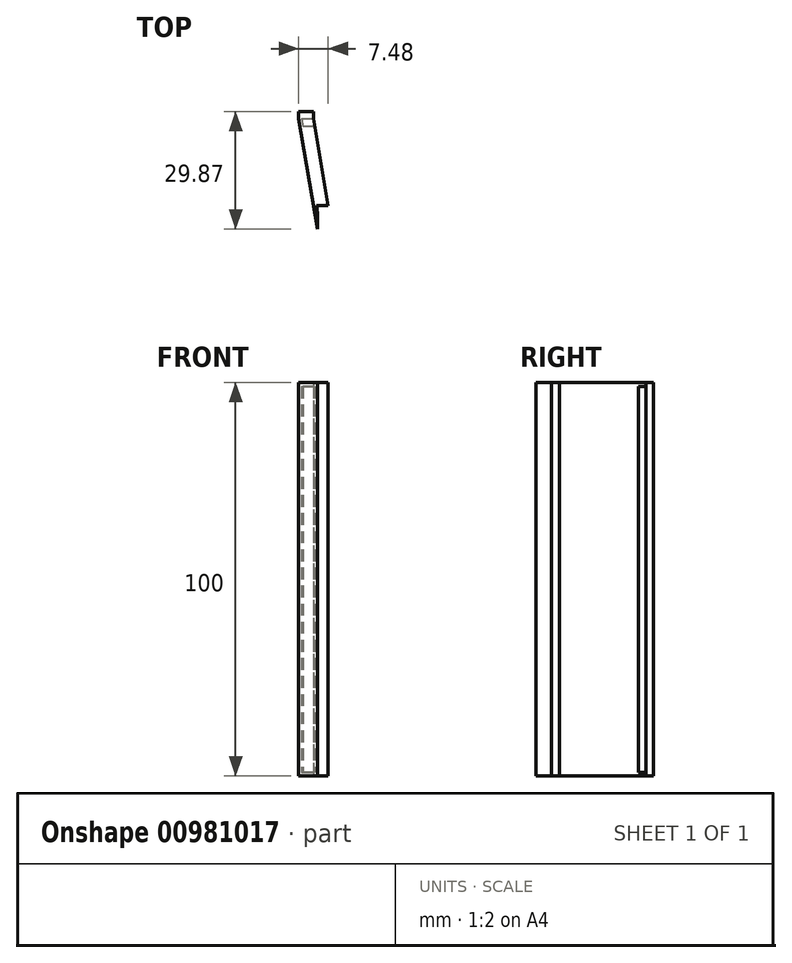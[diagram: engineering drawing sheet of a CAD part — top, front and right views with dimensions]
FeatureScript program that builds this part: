
annotation { "Feature Type Name" : "Feature", "Feature Type Description" : "" }
export const myFeature = defineFeature(function(context is Context, id is Id, definition is map)
    precondition{}
    {
        {
            var Q0;
            Q0=qCreatedBy(makeId("Top.planeOp"),FACE);
            var sketch = newSketch(context, id + "F0", { "sketchPlane" : qUnion([Q0])});
            skLineSegment(sketch, "E0.bottom", {"start": v(-12.5, 2) * mm, "end": v(12.5, 2) * mm});
            skLineSegment(sketch, "E0.top", {"start": v(-12.5, -2) * mm, "end": v(12.5, -2) * mm});
            skLineSegment(sketch, "E0.left", {"start": v(-12.5, 2) * mm, "end": v(-12.5, -2) * mm});
            skLineSegment(sketch, "E0.right", {"start": v(12.5, 2) * mm, "end": v(12.5, -2) * mm});
            skPoint(sketch, "E0.middle", {"position": v(0, 0) * mm});
            skLineSegment(sketch, "E1.left", {"start": v(21.15, 10.87) * mm, "end": v(21.15, 15.48) * mm});
            skLineSegment(sketch, "E2", {"start": v(-5.5, 2) * mm, "end": v(-5.5, -2) * mm});
            skLineSegment(sketch, "E3", {"start": v(-5.5, -2) * mm, "end": v(-3.5, -2) * mm});
            skLineSegment(sketch, "E4", {"start": v(-3.5, -2) * mm, "end": v(-3.5, 2) * mm});
            skLineSegment(sketch, "E5", {"start": v(-3.5, 2) * mm, "end": v(-1.5, 2) * mm});
            skLineSegment(sketch, "E6", {"start": v(-1.5, 2) * mm, "end": v(-1.5, -2) * mm});
            skLineSegment(sketch, "E7", {"start": v(-1.5, -2) * mm, "end": v(0.5, -2) * mm});
            skLineSegment(sketch, "E8", {"start": v(0.5, -2) * mm, "end": v(0.5, 2) * mm});
            skLineSegment(sketch, "E9", {"start": v(0.5, 2) * mm, "end": v(2.5, 2) * mm});
            skLineSegment(sketch, "E10", {"start": v(2.5, 2) * mm, "end": v(2.5, -2) * mm});
            skLineSegment(sketch, "E11", {"start": v(2.5, -2) * mm, "end": v(4.5, -2) * mm});
            skLineSegment(sketch, "E12", {"start": v(4.5, -2) * mm, "end": v(4.5, 2) * mm});
            skLineSegment(sketch, "E13", {"start": v(4.5, 2) * mm, "end": v(6.5, 2) * mm});
            skLineSegment(sketch, "E14", {"start": v(6.5, 2) * mm, "end": v(6.5, -2) * mm});
            skLineSegment(sketch, "E15", {"start": v(0, -2) * mm, "end": v(6.5, -2) * mm});
            skLineSegment(sketch, "E16", {"start": v(0, -2) * mm, "end": v(0, 2) * mm});
            skLineSegment(sketch, "E17", {"start": v(0, 2) * mm, "end": v(8.5, 2) * mm});
            skLineSegment(sketch, "E18", {"start": v(8.5, 2) * mm, "end": v(8.5, -2) * mm});
            skLineSegment(sketch, "E19", {"start": v(8.5, -2) * mm, "end": v(10.5, -2) * mm});
            skLineSegment(sketch, "E20", {"start": v(10.5, -2) * mm, "end": v(10.5, 2) * mm});
            skLineSegment(sketch, "E21", {"start": v(-7.5, 2) * mm, "end": v(-7.5, -2) * mm});
            skLineSegment(sketch, "E22", {"start": v(-7.5, -2) * mm, "end": v(-9.5, -2) * mm});
            skLineSegment(sketch, "E23", {"start": v(-9.5, -2) * mm, "end": v(-9.5, 2) * mm});
            skLineSegment(sketch, "E24", {"start": v(-9.5, 2) * mm, "end": v(-10.4, 2) * mm});
            skLineSegment(sketch, "E25", {"start": v(-12.5, -1.2) * mm, "end": v(12.5, -1.2) * mm});
            skLineSegment(sketch, "E26", {"start": v(-12.5, -2) * mm, "end": v(-17.32, 26) * mm});
            skLineSegment(sketch, "E27", {"start": v(-17.32, 26) * mm, "end": v(-13.63, 26) * mm});
            skLineSegment(sketch, "E28", {"start": v(-13.63, 26) * mm, "end": v(-9.5, 2) * mm});
            skLineSegment(sketch, "E29", {"start": v(-13.29, 24) * mm, "end": v(-16.98, 24) * mm});
            skLineSegment(sketch, "E30", {"start": v(-16.98, 24) * mm, "end": v(-16.63, 22) * mm});
            skLineSegment(sketch, "E31", {"start": v(-16.63, 22) * mm, "end": v(-12.94, 22) * mm});
            skLineSegment(sketch, "E32", {"start": v(-12.94, 22) * mm, "end": v(-12.6, 20) * mm});
            skLineSegment(sketch, "E33", {"start": v(-15.94, 18) * mm, "end": v(-12.25, 18) * mm});
            skLineSegment(sketch, "E34", {"start": v(-12.25, 18) * mm, "end": v(-11.57, 14) * mm});
            skPoint(sketch, "E35.endSnap0", {"position": v(-14.9, 12) * mm});
            skLineSegment(sketch, "E36", {"start": v(-16.29, 20) * mm, "end": v(-12.6, 20) * mm});
            skLineSegment(sketch, "E37", {"start": v(-15.6, 16) * mm, "end": v(-8.68, 16) * mm});
            skLineSegment(sketch, "E38", {"start": v(-15.25, 14) * mm, "end": v(-11.57, 14) * mm});
            skLineSegment(sketch, "E39", {"start": v(-14.9, 12) * mm, "end": v(-11.22, 12) * mm});
            skLineSegment(sketch, "E40", {"start": v(-11.22, 12) * mm, "end": v(-14.9, 12) * mm});
            skLineSegment(sketch, "E41", {"start": v(-14.57, 10) * mm, "end": v(-10.88, 10) * mm});
            skLineSegment(sketch, "E42", {"start": v(-14.22, 8) * mm, "end": v(-10.53, 8) * mm});
            skLineSegment(sketch, "E43", {"start": v(-13.88, 6) * mm, "end": v(-10.19, 6) * mm});
            skLineSegment(sketch, "E44", {"start": v(-13.53, 4) * mm, "end": v(-9.84, 4) * mm});
            skLineSegment(sketch, "E45", {"start": v(-16.63, 26) * mm, "end": v(-12.5, 2) * mm});
            skLineSegment(sketch, "E46", {"start": v(-17.32, 26) * mm, "end": v(-17.32, 27.87) * mm});
            skLineSegment(sketch, "E47", {"start": v(-17.32, 27.87) * mm, "end": v(-13.63, 27.87) * mm});
            skLineSegment(sketch, "E48", {"start": v(-13.63, 27.87) * mm, "end": v(-13.63, 26) * mm});
            skLineSegment(sketch, "E49", {"start": v(12.5, 2) * mm, "end": v(14.56, 2) * mm});
            skLineSegment(sketch, "E50", {"start": v(14.56, 2) * mm, "end": v(12.5, -2) * mm});
            skLineSegment(sketch, "E51", {"start": v(12.5, 0) * mm, "end": v(11.88, -1.2) * mm});
            skLineSegment(sketch, "E52", {"start": v(-9.5, 1.14) * mm, "end": v(-7.5, 1.14) * mm});
            skLineSegment(sketch, "E53", {"start": v(-13.1, 28.79) * mm, "end": v(-8.66, 3) * mm});
            skLineSegment(sketch, "E54", {"start": v(-8.66, 3) * mm, "end": v(16.32, 3) * mm});
            skLineSegment(sketch, "E55", {"start": v(12.5, -3) * mm, "end": v(-13.34, -3) * mm});
            skLineSegment(sketch, "E56", {"start": v(-13.34, -3) * mm, "end": v(-18.81, 28.79) * mm});
            skLineSegment(sketch, "E57", {"start": v(-18.81, 28.79) * mm, "end": v(-13.1, 28.79) * mm});
            skLineSegment(sketch, "E58", {"start": v(16.32, 3) * mm, "end": v(12.5, -3) * mm});
            skSolve(sketch);
        }
        {
            var Q0;
            {var subQ0=sQuery(id+"F0.wireOp",EDGE,"E24");Q0=makeQuery(id+"F0.imprint","IMPRINT",FACE,{"disambiguationData":[TD([[makeQuery(id+"F0.imprint","IMPRINT",EDGE,{"derivedFrom":subQ0}),1.0]])]});}
            var Q1;
            {var subQ0=sQuery(id+"F0.wireOp",EDGE,"E44");var subQ1=sQuery(id+"F0.wireOp",EDGE,"E26");var subQ2=makeQuery(id+"F0.imprint","INTERSECT",VERTEX,{"derivedFrom":[subQ1,subQ0]});Q1=makeQuery(id+"F0.imprint","IMPRINT",FACE,{"disambiguationData":[TD([[makeQuery(id+"F0.imprint","IMPRINT",EDGE,{"disambiguationData":[TD([[subQ2,-1.0]])],"derivedFrom":subQ0}),-1.0]])]});}
            var Q2;
            {var subQ5=sQuery(id+"F0.wireOp",EDGE,"E24");Q2=makeQuery(id+"F0.imprint","IMPRINT",FACE,{"disambiguationData":[TD([[makeQuery(id+"F0.imprint","IMPRINT",EDGE,{"derivedFrom":subQ5}),-1.0]])]});}
            var Q3;
            {var subQ0=sQuery(id+"F0.wireOp",EDGE,"E43");var subQ1=sQuery(id+"F0.wireOp",EDGE,"E26");var subQ2=makeQuery(id+"F0.imprint","INTERSECT",VERTEX,{"derivedFrom":[subQ1,subQ0]});Q3=makeQuery(id+"F0.imprint","IMPRINT",FACE,{"disambiguationData":[TD([[makeQuery(id+"F0.imprint","IMPRINT",EDGE,{"disambiguationData":[TD([[subQ2,1.0]])],"derivedFrom":subQ1}),-1.0]])]});}
            var Q4;
            {var subQ0=sQuery(id+"F0.wireOp",EDGE,"E42");var subQ1=sQuery(id+"F0.wireOp",EDGE,"E28");var subQ2=makeQuery(id+"F0.imprint","INTERSECT",VERTEX,{"derivedFrom":[subQ1,subQ0]});Q4=makeQuery(id+"F0.imprint","IMPRINT",FACE,{"disambiguationData":[TD([[makeQuery(id+"F0.imprint","IMPRINT",EDGE,{"disambiguationData":[TD([[subQ2,-1.0]])],"derivedFrom":subQ1}),-1.0]])]});}
            var Q5;
            {var subQ0=sQuery(id+"F0.wireOp",EDGE,"E42");var subQ1=sQuery(id+"F0.wireOp",EDGE,"E26");var subQ2=makeQuery(id+"F0.imprint","INTERSECT",VERTEX,{"derivedFrom":[subQ1,subQ0]});Q5=makeQuery(id+"F0.imprint","IMPRINT",FACE,{"disambiguationData":[TD([[makeQuery(id+"F0.imprint","IMPRINT",EDGE,{"disambiguationData":[TD([[subQ2,1.0]])],"derivedFrom":subQ1}),-1.0]])]});}
            var Q6;
            {var subQ0=sQuery(id+"F0.wireOp",EDGE,"E41");var subQ1=sQuery(id+"F0.wireOp",EDGE,"E26");var subQ2=makeQuery(id+"F0.imprint","INTERSECT",VERTEX,{"derivedFrom":[subQ1,subQ0]});Q6=makeQuery(id+"F0.imprint","IMPRINT",FACE,{"disambiguationData":[TD([[makeQuery(id+"F0.imprint","IMPRINT",EDGE,{"disambiguationData":[TD([[subQ2,1.0]])],"derivedFrom":subQ1}),-1.0]])]});}
            var Q7;
            {var subQ0=sQuery(id+"F0.wireOp",EDGE,"E40");var subQ1=sQuery(id+"F0.wireOp",EDGE,"E28");var subQ2=makeQuery(id+"F0.imprint","INTERSECT",VERTEX,{"derivedFrom":[subQ1,subQ0]});Q7=makeQuery(id+"F0.imprint","IMPRINT",FACE,{"disambiguationData":[TD([[makeQuery(id+"F0.imprint","IMPRINT",EDGE,{"disambiguationData":[TD([[subQ2,-1.0]])],"derivedFrom":subQ1}),-1.0]])]});}
            var Q8;
            {var subQ1=sQuery(id+"F0.wireOp",EDGE,"E34");var subQ3=sQuery(id+"F0.wireOp",EDGE,"E37");var subQ4=makeQuery(id+"F0.imprint","INTERSECT",VERTEX,{"derivedFrom":[subQ1,subQ3]});Q8=makeQuery(id+"F0.imprint","IMPRINT",FACE,{"disambiguationData":[TD([[makeQuery(id+"F0.imprint","IMPRINT",EDGE,{"disambiguationData":[TD([[subQ4,1.0]])],"derivedFrom":subQ3}),-1.0]])]});}
            var Q9;
            {var subQ3=sQuery(id+"F0.wireOp",EDGE,"E33");var subQ5=sQuery(id+"F0.wireOp",EDGE,"E45");var subQ6=makeQuery(id+"F0.imprint","INTERSECT",VERTEX,{"derivedFrom":[subQ3,subQ5]});Q9=makeQuery(id+"F0.imprint","IMPRINT",FACE,{"disambiguationData":[TD([[makeQuery(id+"F0.imprint","IMPRINT",EDGE,{"disambiguationData":[TD([[subQ6,1.0]])],"derivedFrom":subQ5}),1.0]])]});}
            var Q10;
            {var subQ0=sQuery(id+"F0.wireOp",EDGE,"E40");var subQ1=sQuery(id+"F0.wireOp",EDGE,"E26");var subQ2=makeQuery(id+"F0.imprint","INTERSECT",VERTEX,{"derivedFrom":[subQ1,subQ0]});Q10=makeQuery(id+"F0.imprint","IMPRINT",FACE,{"disambiguationData":[TD([[makeQuery(id+"F0.imprint","IMPRINT",EDGE,{"disambiguationData":[TD([[subQ2,1.0]])],"derivedFrom":subQ1}),-1.0]])]});}
            var Q11;
            {var subQ0=sQuery(id+"F0.wireOp",EDGE,"E38");var subQ1=sQuery(id+"F0.wireOp",EDGE,"E26");var subQ2=makeQuery(id+"F0.imprint","INTERSECT",VERTEX,{"derivedFrom":[subQ1,subQ0]});Q11=makeQuery(id+"F0.imprint","IMPRINT",FACE,{"disambiguationData":[TD([[makeQuery(id+"F0.imprint","IMPRINT",EDGE,{"disambiguationData":[TD([[subQ2,1.0]])],"derivedFrom":subQ1}),-1.0]])]});}
            var Q12;
            {var subQ0=sQuery(id+"F0.wireOp",EDGE,"E37");var subQ1=sQuery(id+"F0.wireOp",EDGE,"E26");var subQ2=makeQuery(id+"F0.imprint","INTERSECT",VERTEX,{"derivedFrom":[subQ1,subQ0]});Q12=makeQuery(id+"F0.imprint","IMPRINT",FACE,{"disambiguationData":[TD([[makeQuery(id+"F0.imprint","IMPRINT",EDGE,{"disambiguationData":[TD([[subQ2,1.0]])],"derivedFrom":subQ1}),-1.0]])]});}
            var Q13;
            {var subQ0=sQuery(id+"F0.wireOp",EDGE,"E33");var subQ1=sQuery(id+"F0.wireOp",EDGE,"E26");var subQ2=makeQuery(id+"F0.imprint","INTERSECT",VERTEX,{"derivedFrom":[subQ1,subQ0]});Q13=makeQuery(id+"F0.imprint","IMPRINT",FACE,{"disambiguationData":[TD([[makeQuery(id+"F0.imprint","IMPRINT",EDGE,{"disambiguationData":[TD([[subQ2,1.0]])],"derivedFrom":subQ1}),-1.0]])]});}
            var Q14;
            {var subQ0=sQuery(id+"F0.wireOp",EDGE,"E33");var subQ1=sQuery(id+"F0.wireOp",EDGE,"E26");var subQ2=makeQuery(id+"F0.imprint","INTERSECT",VERTEX,{"derivedFrom":[subQ1,subQ0]});Q14=makeQuery(id+"F0.imprint","IMPRINT",FACE,{"disambiguationData":[TD([[makeQuery(id+"F0.imprint","IMPRINT",EDGE,{"disambiguationData":[TD([[subQ2,-1.0]])],"derivedFrom":subQ1}),-1.0]])]});}
            var Q15;
            {var subQ1=sQuery(id+"F0.wireOp",EDGE,"E26");var subQ3=sQuery(id+"F0.wireOp",EDGE,"E36");var subQ4=makeQuery(id+"F0.imprint","INTERSECT",VERTEX,{"derivedFrom":[subQ1,subQ3]});Q15=makeQuery(id+"F0.imprint","IMPRINT",FACE,{"disambiguationData":[TD([[makeQuery(id+"F0.imprint","IMPRINT",EDGE,{"disambiguationData":[TD([[subQ4,-1.0]])],"derivedFrom":subQ3}),1.0]])]});}
            var Q16;
            {var subQ0=sQuery(id+"F0.wireOp",EDGE,"E30");Q16=makeQuery(id+"F0.imprint","IMPRINT",FACE,{"disambiguationData":[TD([[makeQuery(id+"F0.imprint","IMPRINT",EDGE,{"derivedFrom":subQ0}),1.0]])]});}
            var Q17;
            {var subQ0=sQuery(id+"F0.wireOp",EDGE,"E27");var subQ5=sQuery(id+"F0.wireOp",EDGE,"E45");var subQ6=makeQuery(id+"F0.imprint","INTERSECT",VERTEX,{"derivedFrom":[subQ0,subQ5]});Q17=makeQuery(id+"F0.imprint","IMPRINT",FACE,{"disambiguationData":[TD([[makeQuery(id+"F0.imprint","IMPRINT",EDGE,{"disambiguationData":[TD([[subQ6,-1.0]])],"derivedFrom":subQ5}),-1.0]])]});}
            var Q18;
            {var subQ0=sQuery(id+"F0.wireOp",EDGE,"E46");Q18=makeQuery(id+"F0.imprint","IMPRINT",FACE,{"disambiguationData":[TD([[makeQuery(id+"F0.imprint","IMPRINT",EDGE,{"derivedFrom":subQ0}),-1.0]])]});}
            var Q19;
            {var subQ0=sQuery(id+"F0.wireOp",EDGE,"E29");var subQ1=sQuery(id+"F0.wireOp",EDGE,"E28");var subQ2=makeQuery(id+"F0.imprint","INTERSECT",VERTEX,{"derivedFrom":[subQ1,subQ0]});Q19=makeQuery(id+"F0.imprint","IMPRINT",FACE,{"disambiguationData":[TD([[makeQuery(id+"F0.imprint","IMPRINT",EDGE,{"disambiguationData":[TD([[subQ2,-1.0]])],"derivedFrom":subQ0}),1.0]])]});}
            extrude(context, id + "F1", {"entities" : qUnion([Q0, Q1, Q2, Q3, Q4, Q5, Q6, Q7, Q8, Q9, Q10, Q11, Q12, Q13, Q14, Q15, Q16, Q17, Q18, Q19]), "depth" : 100 * mm, "offsetDistance" : 25 * mm});
        }
        {
            var Q0;
            {var subQ0=sQuery(id+"F0.wireOp",EDGE,"E33");var subQ1=sQuery(id+"F0.wireOp",EDGE,"E26");var subQ2=makeQuery(id+"F0.imprint","INTERSECT",VERTEX,{"derivedFrom":[subQ1,subQ0]});Q0=makeQuery(id+"F0.imprint","IMPRINT",FACE,{"disambiguationData":[TD([[makeQuery(id+"F0.imprint","IMPRINT",EDGE,{"disambiguationData":[TD([[subQ2,1.0]])],"derivedFrom":subQ1}),-1.0]])]});}
            var Q1;
            {var subQ0=sQuery(id+"F0.wireOp",EDGE,"E34");var subQ5=sQuery(id+"F0.wireOp",EDGE,"E37");var subQ6=makeQuery(id+"F0.imprint","INTERSECT",VERTEX,{"derivedFrom":[subQ0,subQ5]});Q1=makeQuery(id+"F0.imprint","IMPRINT",FACE,{"disambiguationData":[TD([[makeQuery(id+"F0.imprint","IMPRINT",EDGE,{"disambiguationData":[TD([[subQ6,1.0]])],"derivedFrom":subQ5}),1.0]])]});}
            var Q2;
            {var subQ3=sQuery(id+"F0.wireOp",EDGE,"E33");var subQ5=sQuery(id+"F0.wireOp",EDGE,"E45");var subQ6=makeQuery(id+"F0.imprint","INTERSECT",VERTEX,{"derivedFrom":[subQ3,subQ5]});Q2=makeQuery(id+"F0.imprint","IMPRINT",FACE,{"disambiguationData":[TD([[makeQuery(id+"F0.imprint","IMPRINT",EDGE,{"disambiguationData":[TD([[subQ6,1.0]])],"derivedFrom":subQ5}),1.0]])]});}
            var Q3;
            {var subQ0=sQuery(id+"F0.wireOp",EDGE,"E33");var subQ1=sQuery(id+"F0.wireOp",EDGE,"E26");var subQ2=makeQuery(id+"F0.imprint","INTERSECT",VERTEX,{"derivedFrom":[subQ1,subQ0]});Q3=makeQuery(id+"F0.imprint","IMPRINT",FACE,{"disambiguationData":[TD([[makeQuery(id+"F0.imprint","IMPRINT",EDGE,{"disambiguationData":[TD([[subQ2,-1.0]])],"derivedFrom":subQ1}),-1.0]])]});}
            var Q4;
            {var subQ0=sQuery(id+"F0.wireOp",EDGE,"E32");Q4=makeQuery(id+"F0.imprint","IMPRINT",FACE,{"disambiguationData":[TD([[makeQuery(id+"F0.imprint","IMPRINT",EDGE,{"derivedFrom":subQ0}),-1.0]])]});}
            var Q5;
            {var subQ1=sQuery(id+"F0.wireOp",EDGE,"E26");var subQ3=sQuery(id+"F0.wireOp",EDGE,"E36");var subQ4=makeQuery(id+"F0.imprint","INTERSECT",VERTEX,{"derivedFrom":[subQ1,subQ3]});Q5=makeQuery(id+"F0.imprint","IMPRINT",FACE,{"disambiguationData":[TD([[makeQuery(id+"F0.imprint","IMPRINT",EDGE,{"disambiguationData":[TD([[subQ4,-1.0]])],"derivedFrom":subQ3}),1.0]])]});}
            var Q6;
            {var subQ0=sQuery(id+"F0.wireOp",EDGE,"E28");var subQ5=sQuery(id+"F0.wireOp",EDGE,"E29");var subQ6=makeQuery(id+"F0.imprint","INTERSECT",VERTEX,{"derivedFrom":[subQ0,subQ5]});Q6=makeQuery(id+"F0.imprint","IMPRINT",FACE,{"disambiguationData":[TD([[makeQuery(id+"F0.imprint","IMPRINT",EDGE,{"disambiguationData":[TD([[subQ6,-1.0]])],"derivedFrom":subQ5}),-1.0]])]});}
            var Q7;
            {var subQ0=sQuery(id+"F0.wireOp",EDGE,"E29");var subQ1=sQuery(id+"F0.wireOp",EDGE,"E28");var subQ2=makeQuery(id+"F0.imprint","INTERSECT",VERTEX,{"derivedFrom":[subQ1,subQ0]});Q7=makeQuery(id+"F0.imprint","IMPRINT",FACE,{"disambiguationData":[TD([[makeQuery(id+"F0.imprint","IMPRINT",EDGE,{"disambiguationData":[TD([[subQ2,-1.0]])],"derivedFrom":subQ0}),1.0]])]});}
            var Q8;
            {var subQ0=sQuery(id+"F0.wireOp",EDGE,"E30");Q8=makeQuery(id+"F0.imprint","IMPRINT",FACE,{"disambiguationData":[TD([[makeQuery(id+"F0.imprint","IMPRINT",EDGE,{"derivedFrom":subQ0}),1.0]])]});}
            var Q9;
            {var subQ0=sQuery(id+"F0.wireOp",EDGE,"E27");var subQ5=sQuery(id+"F0.wireOp",EDGE,"E45");var subQ6=makeQuery(id+"F0.imprint","INTERSECT",VERTEX,{"derivedFrom":[subQ0,subQ5]});Q9=makeQuery(id+"F0.imprint","IMPRINT",FACE,{"disambiguationData":[TD([[makeQuery(id+"F0.imprint","IMPRINT",EDGE,{"disambiguationData":[TD([[subQ6,-1.0]])],"derivedFrom":subQ5}),-1.0]])]});}
            var Q10;
            {var subQ0=sQuery(id+"F0.wireOp",EDGE,"E46");Q10=makeQuery(id+"F0.imprint","IMPRINT",FACE,{"disambiguationData":[TD([[makeQuery(id+"F0.imprint","IMPRINT",EDGE,{"derivedFrom":subQ0}),-1.0]])]});}
            var Q11;
            {var subQ1=sQuery(id+"F0.wireOp",EDGE,"E34");var subQ3=sQuery(id+"F0.wireOp",EDGE,"E37");var subQ4=makeQuery(id+"F0.imprint","INTERSECT",VERTEX,{"derivedFrom":[subQ1,subQ3]});Q11=makeQuery(id+"F0.imprint","IMPRINT",FACE,{"disambiguationData":[TD([[makeQuery(id+"F0.imprint","IMPRINT",EDGE,{"disambiguationData":[TD([[subQ4,1.0]])],"derivedFrom":subQ3}),-1.0]])]});}
            var Q12;
            {var subQ0=sQuery(id+"F0.wireOp",EDGE,"E37");var subQ1=sQuery(id+"F0.wireOp",EDGE,"E26");var subQ2=makeQuery(id+"F0.imprint","INTERSECT",VERTEX,{"derivedFrom":[subQ1,subQ0]});Q12=makeQuery(id+"F0.imprint","IMPRINT",FACE,{"disambiguationData":[TD([[makeQuery(id+"F0.imprint","IMPRINT",EDGE,{"disambiguationData":[TD([[subQ2,1.0]])],"derivedFrom":subQ1}),-1.0]])]});}
            var Q13;
            {var subQ0=sQuery(id+"F0.wireOp",EDGE,"E38");var subQ1=sQuery(id+"F0.wireOp",EDGE,"E26");var subQ2=makeQuery(id+"F0.imprint","INTERSECT",VERTEX,{"derivedFrom":[subQ1,subQ0]});Q13=makeQuery(id+"F0.imprint","IMPRINT",FACE,{"disambiguationData":[TD([[makeQuery(id+"F0.imprint","IMPRINT",EDGE,{"disambiguationData":[TD([[subQ2,1.0]])],"derivedFrom":subQ1}),-1.0]])]});}
            var Q14;
            {var subQ1=sQuery(id+"F0.wireOp",EDGE,"E28");var subQ3=sQuery(id+"F0.wireOp",EDGE,"E40");var subQ4=makeQuery(id+"F0.imprint","INTERSECT",VERTEX,{"derivedFrom":[subQ1,subQ3]});Q14=makeQuery(id+"F0.imprint","IMPRINT",FACE,{"disambiguationData":[TD([[makeQuery(id+"F0.imprint","IMPRINT",EDGE,{"disambiguationData":[TD([[subQ4,-1.0]])],"derivedFrom":subQ3}),-1.0]])]});}
            var Q15;
            {var subQ0=sQuery(id+"F0.wireOp",EDGE,"E40");var subQ1=sQuery(id+"F0.wireOp",EDGE,"E28");var subQ2=makeQuery(id+"F0.imprint","INTERSECT",VERTEX,{"derivedFrom":[subQ1,subQ0]});Q15=makeQuery(id+"F0.imprint","IMPRINT",FACE,{"disambiguationData":[TD([[makeQuery(id+"F0.imprint","IMPRINT",EDGE,{"disambiguationData":[TD([[subQ2,-1.0]])],"derivedFrom":subQ1}),-1.0]])]});}
            var Q16;
            {var subQ0=sQuery(id+"F0.wireOp",EDGE,"E41");var subQ1=sQuery(id+"F0.wireOp",EDGE,"E28");var subQ2=makeQuery(id+"F0.imprint","INTERSECT",VERTEX,{"derivedFrom":[subQ1,subQ0]});Q16=makeQuery(id+"F0.imprint","IMPRINT",FACE,{"disambiguationData":[TD([[makeQuery(id+"F0.imprint","IMPRINT",EDGE,{"disambiguationData":[TD([[subQ2,-1.0]])],"derivedFrom":subQ1}),-1.0]])]});}
            var Q17;
            {var subQ0=sQuery(id+"F0.wireOp",EDGE,"E42");var subQ1=sQuery(id+"F0.wireOp",EDGE,"E28");var subQ2=makeQuery(id+"F0.imprint","INTERSECT",VERTEX,{"derivedFrom":[subQ1,subQ0]});Q17=makeQuery(id+"F0.imprint","IMPRINT",FACE,{"disambiguationData":[TD([[makeQuery(id+"F0.imprint","IMPRINT",EDGE,{"disambiguationData":[TD([[subQ2,-1.0]])],"derivedFrom":subQ1}),-1.0]])]});}
            var Q18;
            {var subQ0=sQuery(id+"F0.wireOp",EDGE,"E43");var subQ1=sQuery(id+"F0.wireOp",EDGE,"E28");var subQ2=makeQuery(id+"F0.imprint","INTERSECT",VERTEX,{"derivedFrom":[subQ1,subQ0]});Q18=makeQuery(id+"F0.imprint","IMPRINT",FACE,{"disambiguationData":[TD([[makeQuery(id+"F0.imprint","IMPRINT",EDGE,{"disambiguationData":[TD([[subQ2,-1.0]])],"derivedFrom":subQ1}),-1.0]])]});}
            var Q19;
            {var subQ0=sQuery(id+"F0.wireOp",EDGE,"E43");var subQ1=sQuery(id+"F0.wireOp",EDGE,"E26");var subQ2=makeQuery(id+"F0.imprint","INTERSECT",VERTEX,{"derivedFrom":[subQ1,subQ0]});Q19=makeQuery(id+"F0.imprint","IMPRINT",FACE,{"disambiguationData":[TD([[makeQuery(id+"F0.imprint","IMPRINT",EDGE,{"disambiguationData":[TD([[subQ2,1.0]])],"derivedFrom":subQ1}),-1.0]])]});}
            var Q20;
            {var subQ0=sQuery(id+"F0.wireOp",EDGE,"E42");var subQ1=sQuery(id+"F0.wireOp",EDGE,"E26");var subQ2=makeQuery(id+"F0.imprint","INTERSECT",VERTEX,{"derivedFrom":[subQ1,subQ0]});Q20=makeQuery(id+"F0.imprint","IMPRINT",FACE,{"disambiguationData":[TD([[makeQuery(id+"F0.imprint","IMPRINT",EDGE,{"disambiguationData":[TD([[subQ2,1.0]])],"derivedFrom":subQ1}),-1.0]])]});}
            var Q21;
            {var subQ0=sQuery(id+"F0.wireOp",EDGE,"E41");var subQ1=sQuery(id+"F0.wireOp",EDGE,"E26");var subQ2=makeQuery(id+"F0.imprint","INTERSECT",VERTEX,{"derivedFrom":[subQ1,subQ0]});Q21=makeQuery(id+"F0.imprint","IMPRINT",FACE,{"disambiguationData":[TD([[makeQuery(id+"F0.imprint","IMPRINT",EDGE,{"disambiguationData":[TD([[subQ2,1.0]])],"derivedFrom":subQ1}),-1.0]])]});}
            var Q22;
            {var subQ0=sQuery(id+"F0.wireOp",EDGE,"E40");var subQ1=sQuery(id+"F0.wireOp",EDGE,"E26");var subQ2=makeQuery(id+"F0.imprint","INTERSECT",VERTEX,{"derivedFrom":[subQ1,subQ0]});Q22=makeQuery(id+"F0.imprint","IMPRINT",FACE,{"disambiguationData":[TD([[makeQuery(id+"F0.imprint","IMPRINT",EDGE,{"disambiguationData":[TD([[subQ2,1.0]])],"derivedFrom":subQ1}),-1.0]])]});}
            var Q23;
            {var subQ5=sQuery(id+"F0.wireOp",EDGE,"E24");Q23=makeQuery(id+"F0.imprint","IMPRINT",FACE,{"disambiguationData":[TD([[makeQuery(id+"F0.imprint","IMPRINT",EDGE,{"derivedFrom":subQ5}),-1.0]])]});}
            var Q24;
            {var subQ0=sQuery(id+"F0.wireOp",EDGE,"E44");var subQ1=sQuery(id+"F0.wireOp",EDGE,"E26");var subQ2=makeQuery(id+"F0.imprint","INTERSECT",VERTEX,{"derivedFrom":[subQ1,subQ0]});Q24=makeQuery(id+"F0.imprint","IMPRINT",FACE,{"disambiguationData":[TD([[makeQuery(id+"F0.imprint","IMPRINT",EDGE,{"disambiguationData":[TD([[subQ2,-1.0]])],"derivedFrom":subQ0}),-1.0]])]});}
            extrude(context, id + "F2", {"entities" : qUnion([Q0, Q1, Q2, Q3, Q4, Q5, Q6, Q7, Q8, Q9, Q10, Q11, Q12, Q13, Q14, Q15, Q16, Q17, Q18, Q19, Q20, Q21, Q22, Q23, Q24]), "operationType" : NewBodyOperationType.ADD, "depth" : 1 * mm, "offsetDistance" : 25 * mm});
        }
        {
            var Q0;
            {var subQ0=sQuery(id+"F0.wireOp",EDGE,"E46");Q0=makeQuery(id+"F0.imprint","IMPRINT",FACE,{"disambiguationData":[TD([[makeQuery(id+"F0.imprint","IMPRINT",EDGE,{"derivedFrom":subQ0}),-1.0]])]});}
            var Q1;
            {var subQ0=sQuery(id+"F0.wireOp",EDGE,"E28");var subQ5=sQuery(id+"F0.wireOp",EDGE,"E29");var subQ6=makeQuery(id+"F0.imprint","INTERSECT",VERTEX,{"derivedFrom":[subQ0,subQ5]});Q1=makeQuery(id+"F0.imprint","IMPRINT",FACE,{"disambiguationData":[TD([[makeQuery(id+"F0.imprint","IMPRINT",EDGE,{"disambiguationData":[TD([[subQ6,-1.0]])],"derivedFrom":subQ5}),-1.0]])]});}
            var Q2;
            {var subQ0=sQuery(id+"F0.wireOp",EDGE,"E29");var subQ1=sQuery(id+"F0.wireOp",EDGE,"E28");var subQ2=makeQuery(id+"F0.imprint","INTERSECT",VERTEX,{"derivedFrom":[subQ1,subQ0]});Q2=makeQuery(id+"F0.imprint","IMPRINT",FACE,{"disambiguationData":[TD([[makeQuery(id+"F0.imprint","IMPRINT",EDGE,{"disambiguationData":[TD([[subQ2,-1.0]])],"derivedFrom":subQ0}),1.0]])]});}
            var Q3;
            {var subQ0=sQuery(id+"F0.wireOp",EDGE,"E32");Q3=makeQuery(id+"F0.imprint","IMPRINT",FACE,{"disambiguationData":[TD([[makeQuery(id+"F0.imprint","IMPRINT",EDGE,{"derivedFrom":subQ0}),-1.0]])]});}
            var Q4;
            {var subQ3=sQuery(id+"F0.wireOp",EDGE,"E33");var subQ5=sQuery(id+"F0.wireOp",EDGE,"E45");var subQ6=makeQuery(id+"F0.imprint","INTERSECT",VERTEX,{"derivedFrom":[subQ3,subQ5]});Q4=makeQuery(id+"F0.imprint","IMPRINT",FACE,{"disambiguationData":[TD([[makeQuery(id+"F0.imprint","IMPRINT",EDGE,{"disambiguationData":[TD([[subQ6,1.0]])],"derivedFrom":subQ5}),1.0]])]});}
            var Q5;
            {var subQ0=sQuery(id+"F0.wireOp",EDGE,"E34");var subQ5=sQuery(id+"F0.wireOp",EDGE,"E37");var subQ6=makeQuery(id+"F0.imprint","INTERSECT",VERTEX,{"derivedFrom":[subQ0,subQ5]});Q5=makeQuery(id+"F0.imprint","IMPRINT",FACE,{"disambiguationData":[TD([[makeQuery(id+"F0.imprint","IMPRINT",EDGE,{"disambiguationData":[TD([[subQ6,1.0]])],"derivedFrom":subQ5}),1.0]])]});}
            var Q6;
            {var subQ1=sQuery(id+"F0.wireOp",EDGE,"E34");var subQ3=sQuery(id+"F0.wireOp",EDGE,"E37");var subQ4=makeQuery(id+"F0.imprint","INTERSECT",VERTEX,{"derivedFrom":[subQ1,subQ3]});Q6=makeQuery(id+"F0.imprint","IMPRINT",FACE,{"disambiguationData":[TD([[makeQuery(id+"F0.imprint","IMPRINT",EDGE,{"disambiguationData":[TD([[subQ4,1.0]])],"derivedFrom":subQ3}),-1.0]])]});}
            var Q7;
            {var subQ0=sQuery(id+"F0.wireOp",EDGE,"E33");var subQ1=sQuery(id+"F0.wireOp",EDGE,"E26");var subQ2=makeQuery(id+"F0.imprint","INTERSECT",VERTEX,{"derivedFrom":[subQ1,subQ0]});Q7=makeQuery(id+"F0.imprint","IMPRINT",FACE,{"disambiguationData":[TD([[makeQuery(id+"F0.imprint","IMPRINT",EDGE,{"disambiguationData":[TD([[subQ2,1.0]])],"derivedFrom":subQ1}),-1.0]])]});}
            var Q8;
            {var subQ0=sQuery(id+"F0.wireOp",EDGE,"E33");var subQ1=sQuery(id+"F0.wireOp",EDGE,"E26");var subQ2=makeQuery(id+"F0.imprint","INTERSECT",VERTEX,{"derivedFrom":[subQ1,subQ0]});Q8=makeQuery(id+"F0.imprint","IMPRINT",FACE,{"disambiguationData":[TD([[makeQuery(id+"F0.imprint","IMPRINT",EDGE,{"disambiguationData":[TD([[subQ2,-1.0]])],"derivedFrom":subQ1}),-1.0]])]});}
            var Q9;
            {var subQ1=sQuery(id+"F0.wireOp",EDGE,"E26");var subQ3=sQuery(id+"F0.wireOp",EDGE,"E36");var subQ4=makeQuery(id+"F0.imprint","INTERSECT",VERTEX,{"derivedFrom":[subQ1,subQ3]});Q9=makeQuery(id+"F0.imprint","IMPRINT",FACE,{"disambiguationData":[TD([[makeQuery(id+"F0.imprint","IMPRINT",EDGE,{"disambiguationData":[TD([[subQ4,-1.0]])],"derivedFrom":subQ3}),1.0]])]});}
            var Q10;
            {var subQ0=sQuery(id+"F0.wireOp",EDGE,"E30");Q10=makeQuery(id+"F0.imprint","IMPRINT",FACE,{"disambiguationData":[TD([[makeQuery(id+"F0.imprint","IMPRINT",EDGE,{"derivedFrom":subQ0}),1.0]])]});}
            var Q11;
            {var subQ0=sQuery(id+"F0.wireOp",EDGE,"E27");var subQ5=sQuery(id+"F0.wireOp",EDGE,"E45");var subQ6=makeQuery(id+"F0.imprint","INTERSECT",VERTEX,{"derivedFrom":[subQ0,subQ5]});Q11=makeQuery(id+"F0.imprint","IMPRINT",FACE,{"disambiguationData":[TD([[makeQuery(id+"F0.imprint","IMPRINT",EDGE,{"disambiguationData":[TD([[subQ6,-1.0]])],"derivedFrom":subQ5}),-1.0]])]});}
            var Q12;
            {var subQ0=sQuery(id+"F0.wireOp",EDGE,"E37");var subQ1=sQuery(id+"F0.wireOp",EDGE,"E26");var subQ2=makeQuery(id+"F0.imprint","INTERSECT",VERTEX,{"derivedFrom":[subQ1,subQ0]});Q12=makeQuery(id+"F0.imprint","IMPRINT",FACE,{"disambiguationData":[TD([[makeQuery(id+"F0.imprint","IMPRINT",EDGE,{"disambiguationData":[TD([[subQ2,1.0]])],"derivedFrom":subQ1}),-1.0]])]});}
            var Q13;
            {var subQ0=sQuery(id+"F0.wireOp",EDGE,"E38");var subQ1=sQuery(id+"F0.wireOp",EDGE,"E26");var subQ2=makeQuery(id+"F0.imprint","INTERSECT",VERTEX,{"derivedFrom":[subQ1,subQ0]});Q13=makeQuery(id+"F0.imprint","IMPRINT",FACE,{"disambiguationData":[TD([[makeQuery(id+"F0.imprint","IMPRINT",EDGE,{"disambiguationData":[TD([[subQ2,1.0]])],"derivedFrom":subQ1}),-1.0]])]});}
            var Q14;
            {var subQ1=sQuery(id+"F0.wireOp",EDGE,"E28");var subQ3=sQuery(id+"F0.wireOp",EDGE,"E40");var subQ4=makeQuery(id+"F0.imprint","INTERSECT",VERTEX,{"derivedFrom":[subQ1,subQ3]});Q14=makeQuery(id+"F0.imprint","IMPRINT",FACE,{"disambiguationData":[TD([[makeQuery(id+"F0.imprint","IMPRINT",EDGE,{"disambiguationData":[TD([[subQ4,-1.0]])],"derivedFrom":subQ3}),-1.0]])]});}
            var Q15;
            {var subQ0=sQuery(id+"F0.wireOp",EDGE,"E40");var subQ1=sQuery(id+"F0.wireOp",EDGE,"E28");var subQ2=makeQuery(id+"F0.imprint","INTERSECT",VERTEX,{"derivedFrom":[subQ1,subQ0]});Q15=makeQuery(id+"F0.imprint","IMPRINT",FACE,{"disambiguationData":[TD([[makeQuery(id+"F0.imprint","IMPRINT",EDGE,{"disambiguationData":[TD([[subQ2,-1.0]])],"derivedFrom":subQ1}),-1.0]])]});}
            var Q16;
            {var subQ0=sQuery(id+"F0.wireOp",EDGE,"E40");var subQ1=sQuery(id+"F0.wireOp",EDGE,"E26");var subQ2=makeQuery(id+"F0.imprint","INTERSECT",VERTEX,{"derivedFrom":[subQ1,subQ0]});Q16=makeQuery(id+"F0.imprint","IMPRINT",FACE,{"disambiguationData":[TD([[makeQuery(id+"F0.imprint","IMPRINT",EDGE,{"disambiguationData":[TD([[subQ2,1.0]])],"derivedFrom":subQ1}),-1.0]])]});}
            var Q17;
            {var subQ0=sQuery(id+"F0.wireOp",EDGE,"E41");var subQ1=sQuery(id+"F0.wireOp",EDGE,"E26");var subQ2=makeQuery(id+"F0.imprint","INTERSECT",VERTEX,{"derivedFrom":[subQ1,subQ0]});Q17=makeQuery(id+"F0.imprint","IMPRINT",FACE,{"disambiguationData":[TD([[makeQuery(id+"F0.imprint","IMPRINT",EDGE,{"disambiguationData":[TD([[subQ2,1.0]])],"derivedFrom":subQ1}),-1.0]])]});}
            var Q18;
            {var subQ0=sQuery(id+"F0.wireOp",EDGE,"E41");var subQ1=sQuery(id+"F0.wireOp",EDGE,"E28");var subQ2=makeQuery(id+"F0.imprint","INTERSECT",VERTEX,{"derivedFrom":[subQ1,subQ0]});Q18=makeQuery(id+"F0.imprint","IMPRINT",FACE,{"disambiguationData":[TD([[makeQuery(id+"F0.imprint","IMPRINT",EDGE,{"disambiguationData":[TD([[subQ2,-1.0]])],"derivedFrom":subQ1}),-1.0]])]});}
            var Q19;
            {var subQ0=sQuery(id+"F0.wireOp",EDGE,"E42");var subQ1=sQuery(id+"F0.wireOp",EDGE,"E28");var subQ2=makeQuery(id+"F0.imprint","INTERSECT",VERTEX,{"derivedFrom":[subQ1,subQ0]});Q19=makeQuery(id+"F0.imprint","IMPRINT",FACE,{"disambiguationData":[TD([[makeQuery(id+"F0.imprint","IMPRINT",EDGE,{"disambiguationData":[TD([[subQ2,-1.0]])],"derivedFrom":subQ1}),-1.0]])]});}
            var Q20;
            {var subQ0=sQuery(id+"F0.wireOp",EDGE,"E42");var subQ1=sQuery(id+"F0.wireOp",EDGE,"E26");var subQ2=makeQuery(id+"F0.imprint","INTERSECT",VERTEX,{"derivedFrom":[subQ1,subQ0]});Q20=makeQuery(id+"F0.imprint","IMPRINT",FACE,{"disambiguationData":[TD([[makeQuery(id+"F0.imprint","IMPRINT",EDGE,{"disambiguationData":[TD([[subQ2,1.0]])],"derivedFrom":subQ1}),-1.0]])]});}
            var Q21;
            {var subQ5=sQuery(id+"F0.wireOp",EDGE,"E24");Q21=makeQuery(id+"F0.imprint","IMPRINT",FACE,{"disambiguationData":[TD([[makeQuery(id+"F0.imprint","IMPRINT",EDGE,{"derivedFrom":subQ5}),-1.0]])]});}
            var Q22;
            {var subQ0=sQuery(id+"F0.wireOp",EDGE,"E24");Q22=makeQuery(id+"F0.imprint","IMPRINT",FACE,{"disambiguationData":[TD([[makeQuery(id+"F0.imprint","IMPRINT",EDGE,{"derivedFrom":subQ0}),1.0]])]});}
            var Q23;
            {var subQ0=sQuery(id+"F0.wireOp",EDGE,"E44");var subQ1=sQuery(id+"F0.wireOp",EDGE,"E26");var subQ2=makeQuery(id+"F0.imprint","INTERSECT",VERTEX,{"derivedFrom":[subQ1,subQ0]});Q23=makeQuery(id+"F0.imprint","IMPRINT",FACE,{"disambiguationData":[TD([[makeQuery(id+"F0.imprint","IMPRINT",EDGE,{"disambiguationData":[TD([[subQ2,-1.0]])],"derivedFrom":subQ0}),-1.0]])]});}
            var Q24;
            {var subQ0=sQuery(id+"F0.wireOp",EDGE,"E43");var subQ1=sQuery(id+"F0.wireOp",EDGE,"E26");var subQ2=makeQuery(id+"F0.imprint","INTERSECT",VERTEX,{"derivedFrom":[subQ1,subQ0]});Q24=makeQuery(id+"F0.imprint","IMPRINT",FACE,{"disambiguationData":[TD([[makeQuery(id+"F0.imprint","IMPRINT",EDGE,{"disambiguationData":[TD([[subQ2,1.0]])],"derivedFrom":subQ1}),-1.0]])]});}
            var Q25;
            {var subQ0=sQuery(id+"F0.wireOp",EDGE,"E43");var subQ1=sQuery(id+"F0.wireOp",EDGE,"E28");var subQ2=makeQuery(id+"F0.imprint","INTERSECT",VERTEX,{"derivedFrom":[subQ1,subQ0]});Q25=makeQuery(id+"F0.imprint","IMPRINT",FACE,{"disambiguationData":[TD([[makeQuery(id+"F0.imprint","IMPRINT",EDGE,{"disambiguationData":[TD([[subQ2,-1.0]])],"derivedFrom":subQ1}),-1.0]])]});}
            extrude(context, id + "F3", {"entities" : qUnion([Q0, Q1, Q2, Q3, Q4, Q5, Q6, Q7, Q8, Q9, Q10, Q11, Q12, Q13, Q14, Q15, Q16, Q17, Q18, Q19, Q20, Q21, Q22, Q23, Q24, Q25]), "operationType" : NewBodyOperationType.ADD, "depth" : 100 * mm, "offsetDistance" : 25 * mm, "hasSecondDirection" : true, "secondDirectionOppositeDirection" : false, "secondDirectionDepth" : 99 * mm});
        }
    });
